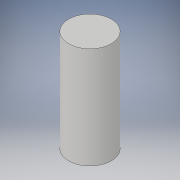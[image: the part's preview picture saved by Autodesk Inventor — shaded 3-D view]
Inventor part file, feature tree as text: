
AUTODESK INVENTOR PART (.ipt)
format: ipt  version: 2019 (Build 230136000, 136)  size: 88,576 bytes
history: native  units: mm
features: extrude x1, sketch x1
ambient origin geometry x8: Origin, YZ Plane, XZ Plane, XY Plane, X Axis, Y Axis, Z Axis, Center Point
bodies: Solid1 (feature_tree)
feature tree (2):
  extrude  "Extrusion1"  Depth=100.0mm TaperAngle=0.0deg
  sketch  "Sketch1"  dims[d0=42.0mm d1=100.0mm d2=0.0mm]
